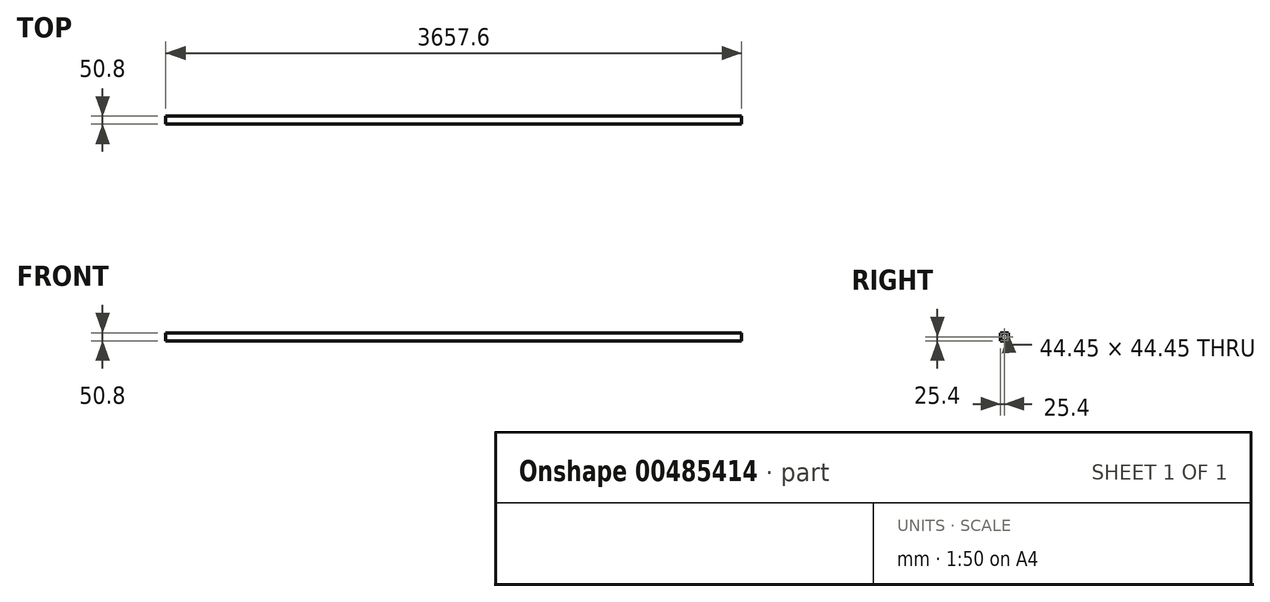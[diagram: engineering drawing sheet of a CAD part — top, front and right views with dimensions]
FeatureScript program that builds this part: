
annotation { "Feature Type Name" : "Feature", "Feature Type Description" : "" }
export const myFeature = defineFeature(function(context is Context, id is Id, definition is map)
    precondition{}
    {
        {
            var Q0;
            Q0=qCreatedBy(makeId("Right.planeOp"),FACE);
            var sketch = newSketch(context, id + "F0", { "sketchPlane" : qUnion([Q0])});
            skLineSegment(sketch, "E0.bottom", {"start": v(25.4, 25.4) * mm, "end": v(-25.4, 25.4) * mm});
            skLineSegment(sketch, "E0.top", {"start": v(25.4, -25.4) * mm, "end": v(-25.4, -25.4) * mm});
            skLineSegment(sketch, "E0.left", {"start": v(25.4, 25.4) * mm, "end": v(25.4, -25.4) * mm});
            skLineSegment(sketch, "E0.right", {"start": v(-25.4, 25.4) * mm, "end": v(-25.4, -25.4) * mm});
            skPoint(sketch, "E0.middle", {"position": v(0, 0) * mm});
            skLineSegment(sketch, "E1.bottom", {"start": v(22.22, 22.23) * mm, "end": v(-22.23, 22.22) * mm});
            skLineSegment(sketch, "E1.top", {"start": v(22.23, -22.22) * mm, "end": v(-22.22, -22.23) * mm});
            skLineSegment(sketch, "E1.left", {"start": v(22.22, 22.23) * mm, "end": v(22.23, -22.22) * mm});
            skLineSegment(sketch, "E1.right", {"start": v(-22.23, 22.22) * mm, "end": v(-22.22, -22.23) * mm});
            skSolve(sketch);
        }
        {
            var Q0;
            Q0=makeQuery(id+"F0.imprint","IMPRINT",FACE,{"disambiguationData":[TD([[makeQuery(id+"F0.imprint","IMPRINT",EDGE,{"derivedFrom":sQuery(id+"F0.wireOp",EDGE,"E0.bottom")}),1.0]])]});
            extrude(context, id + "F1", {"entities" : qUnion([Q0]), "depth" : 3657.6 * mm});
        }
    });
